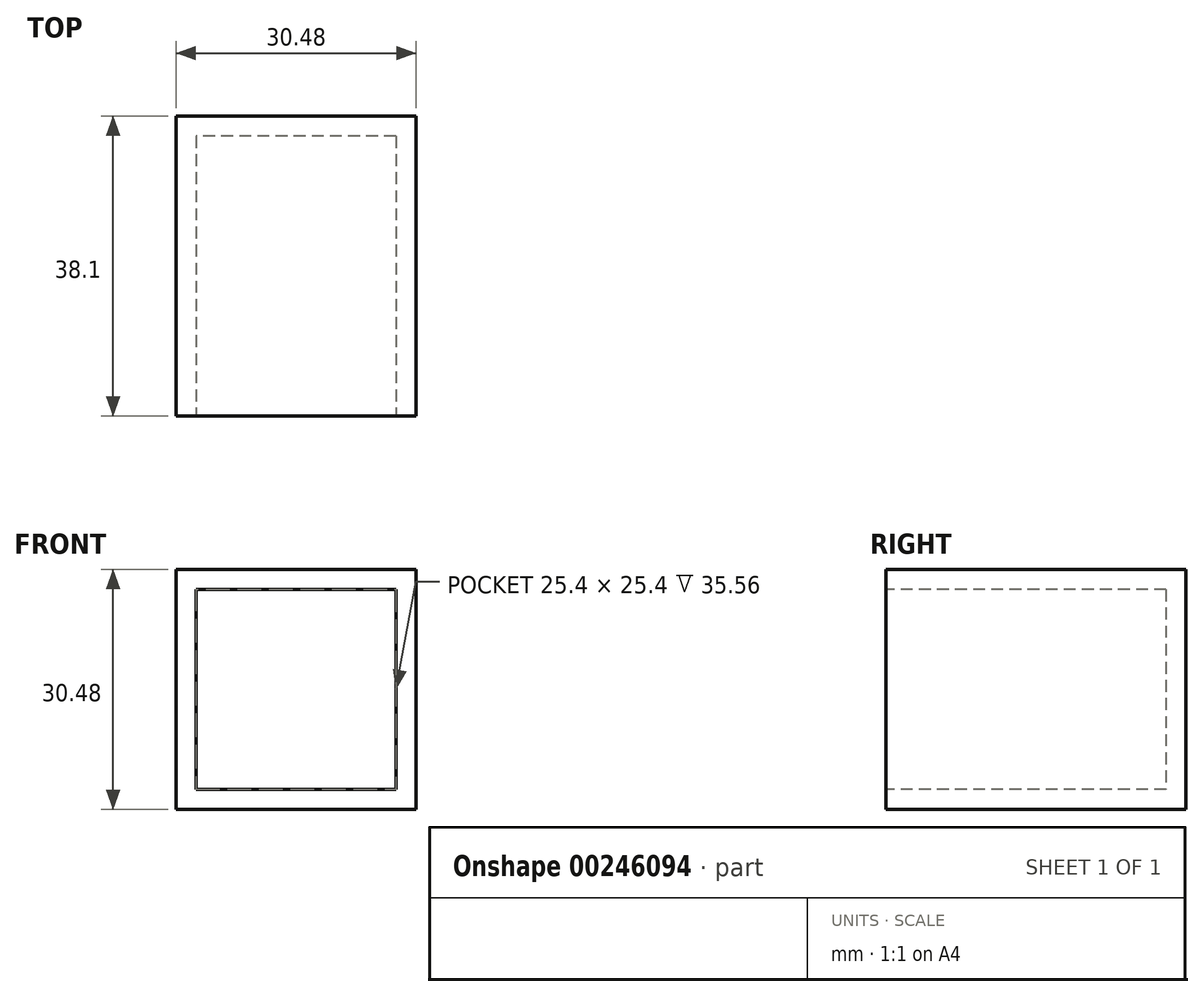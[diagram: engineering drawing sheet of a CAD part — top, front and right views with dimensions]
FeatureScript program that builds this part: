
annotation { "Feature Type Name" : "Feature", "Feature Type Description" : "" }
export const myFeature = defineFeature(function(context is Context, id is Id, definition is map)
    precondition{}
    {
        {
            var Q0;
            Q0=qCreatedBy(makeId("Front.planeOp"),FACE);
            var sketch = newSketch(context, id + "F0", { "sketchPlane" : qUnion([Q0])});
            skLineSegment(sketch, "E0", {"start": v(0, 0) * mm, "end": v(0, 30.48) * mm});
            skLineSegment(sketch, "E1", {"start": v(0, 30.48) * mm, "end": v(30.48, 30.48) * mm});
            skLineSegment(sketch, "E2", {"start": v(30.48, 30.48) * mm, "end": v(30.48, 0) * mm});
            skLineSegment(sketch, "E3", {"start": v(30.48, 0) * mm, "end": v(0, 0) * mm});
            skSolve(sketch);
        }
        {
            var Q0;
            Q0=makeQuery(id+"F0.imprint","IMPRINT",FACE,{"disambiguationData":[TD([[makeQuery(id+"F0.imprint","IMPRINT",EDGE,{"derivedFrom":sQuery(id+"F0.wireOp",EDGE,"E0")}),-1.0]])]});
            extrude(context, id + "F1", {"entities" : qUnion([Q0]), "depth" : 38.1 * mm});
        }
        {
            var Q0;
            Q0=makeQuery(id+"F1.opExtrude","CAP_FACE",FACE,{"disambiguationData":[OSD([sQuery(id+"F0.wireOp",EDGE,"E0"),sQuery(id+"F0.wireOp",EDGE,"E1"),sQuery(id+"F0.wireOp",EDGE,"E2"),sQuery(id+"F0.wireOp",EDGE,"E3")])],"isStart":false});
            var sketch = newSketch(context, id + "F2", { "sketchPlane" : qUnion([Q0])});
            skLineSegment(sketch, "E4", {"start": v(2.54, 27.94) * mm, "end": v(2.54, 2.54) * mm});
            skLineSegment(sketch, "E5", {"start": v(2.54, 2.54) * mm, "end": v(27.94, 2.54) * mm});
            skLineSegment(sketch, "E6", {"start": v(27.94, 2.54) * mm, "end": v(27.94, 27.94) * mm});
            skLineSegment(sketch, "E7", {"start": v(27.94, 27.94) * mm, "end": v(2.54, 27.94) * mm});
            skSolve(sketch);
        }
        {
            var Q0;
            Q0=makeQuery(id+"F2.imprint","IMPRINT",FACE,{"disambiguationData":[TD([[makeQuery(id+"F2.imprint","IMPRINT",EDGE,{"derivedFrom":sQuery(id+"F2.wireOp",EDGE,"E4")}),1.0]])]});
            extrude(context, id + "F3", {"entities" : qUnion([Q0]), "operationType" : NewBodyOperationType.REMOVE, "oppositeDirection" : true, "depth" : 35.56 * mm});
        }
    });
